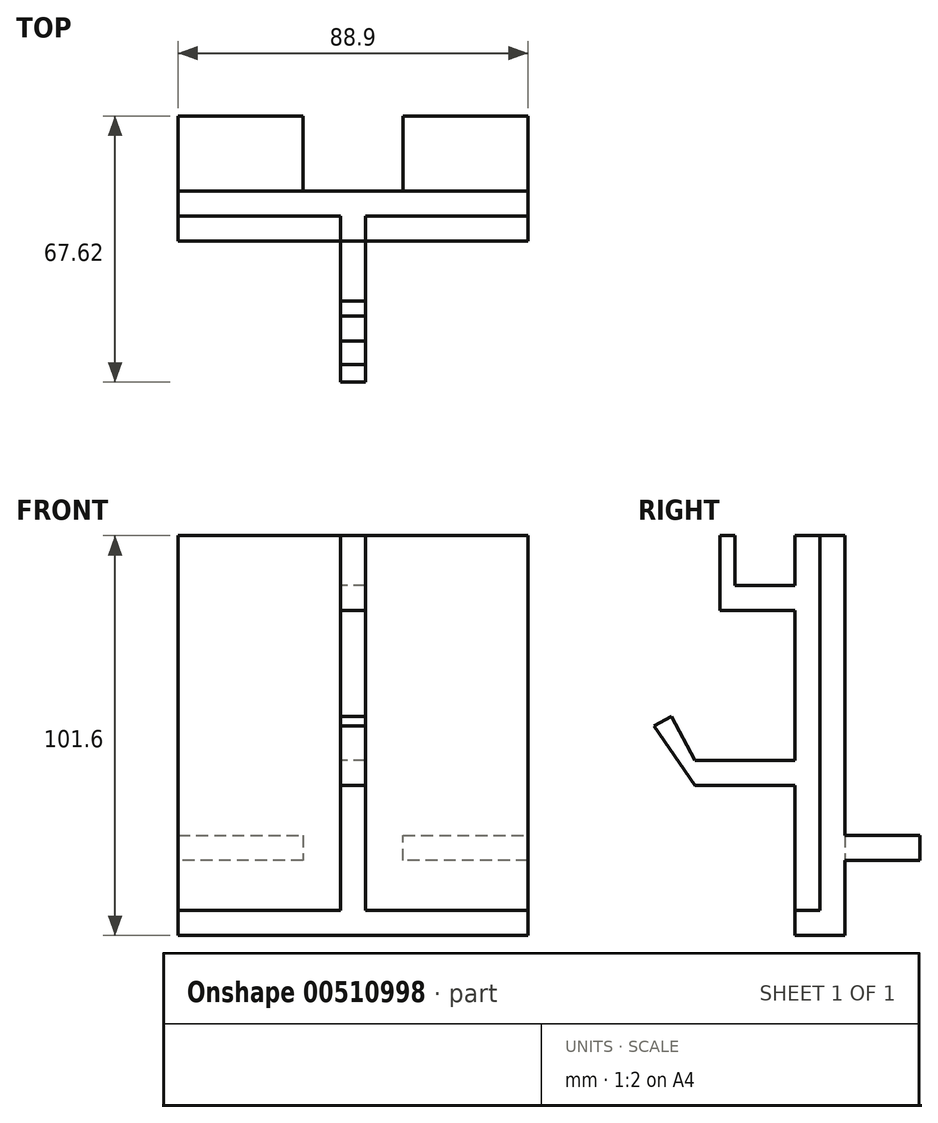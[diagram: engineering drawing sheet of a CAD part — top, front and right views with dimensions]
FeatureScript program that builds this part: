
annotation { "Feature Type Name" : "Feature", "Feature Type Description" : "" }
export const myFeature = defineFeature(function(context is Context, id is Id, definition is map)
    precondition{}
    {
        {
            var Q0;
            Q0=qCreatedBy(makeId("Right.planeOp"),FACE);
            var sketch = newSketch(context, id + "F0", { "sketchPlane" : qUnion([Q0])});
            skLineSegment(sketch, "E0", {"start": v(-3.18, 25.71) * mm, "end": v(-3.17, -75.89) * mm});
            skLineSegment(sketch, "E1", {"start": v(-3.17, -75.89) * mm, "end": v(3.18, -75.89) * mm});
            skLineSegment(sketch, "E2", {"start": v(3.18, -75.89) * mm, "end": v(3.18, 25.71) * mm});
            skLineSegment(sketch, "E3", {"start": v(3.18, 25.71) * mm, "end": v(-3.18, 25.71) * mm});
            skLineSegment(sketch, "E4", {"start": v(-3.17, -31.44) * mm, "end": v(-28.57, -31.44) * mm});
            skLineSegment(sketch, "E5", {"start": v(-28.57, -31.44) * mm, "end": v(-28.57, -37.79) * mm});
            skLineSegment(sketch, "E6", {"start": v(-28.57, -37.79) * mm, "end": v(-3.17, -37.79) * mm});
            skLineSegment(sketch, "E7", {"start": v(-28.57, -31.44) * mm, "end": v(-34.57, -20.24) * mm});
            skLineSegment(sketch, "E8", {"start": v(-34.57, -20.24) * mm, "end": v(-39.05, -22.64) * mm});
            skLineSegment(sketch, "E9", {"start": v(-39.05, -22.64) * mm, "end": v(-28.57, -37.79) * mm});
            skLineSegment(sketch, "E10", {"start": v(-3.18, 13.01) * mm, "end": v(-22.23, 13.01) * mm});
            skLineSegment(sketch, "E11", {"start": v(-22.23, 13.01) * mm, "end": v(-22.23, 6.66) * mm});
            skLineSegment(sketch, "E12", {"start": v(-22.23, 6.66) * mm, "end": v(-3.17, 6.66) * mm});
            skLineSegment(sketch, "E13", {"start": v(-3.18, 6.66) * mm, "end": v(-3.18, 13.01) * mm});
            skSolve(sketch);
        }
        {
            var Q0;
            Q0=makeQuery(id+"F0.imprint","IMPRINT",FACE,{"disambiguationData":[TD([[makeQuery(id+"F0.imprint","IMPRINT",EDGE,{"derivedFrom":sQuery(id+"F0.wireOp",EDGE,"E5")}),-1.0]])]});
            var Q1;
            {var subQ0=sQuery(id+"F0.wireOp",EDGE,"E4");Q1=makeQuery(id+"F0.imprint","IMPRINT",FACE,{"disambiguationData":[TD([[makeQuery(id+"F0.imprint","IMPRINT",EDGE,{"derivedFrom":subQ0}),1.0]])]});}
            var Q2;
            {var subQ0=sQuery(id+"F0.wireOp",EDGE,"E1");Q2=makeQuery(id+"F0.imprint","IMPRINT",FACE,{"disambiguationData":[TD([[makeQuery(id+"F0.imprint","IMPRINT",EDGE,{"derivedFrom":subQ0}),1.0]])]});}
            var Q3;
            Q3=makeQuery(id+"F0.imprint","IMPRINT",FACE,{"disambiguationData":[TD([[makeQuery(id+"F0.imprint","IMPRINT",EDGE,{"derivedFrom":sQuery(id+"F0.wireOp",EDGE,"E10")}),1.0]])]});
            extrude(context, id + "F1", {"entities" : qUnion([Q0, Q1, Q2, Q3]), "depth" : 6.35 * mm, "offsetDistance" : 25.4 * mm});
        }
        {
            var Q0;
            Q0=makeQuery(id+"F1.opExtrude","SWEPT_FACE",FACE,{"disambiguationData":[OSD([sQuery(id+"F0.wireOp",EDGE,"E2")])]});
            var sketch = newSketch(context, id + "F2", { "sketchPlane" : qUnion([Q0])});
            skLineSegment(sketch, "E14", {"start": v(-3.18, 25.71) * mm, "end": v(-47.63, 25.71) * mm});
            skPoint(sketch, "E14.endSnap0", {"position": v(-3.18, 25.71) * mm});
            skLineSegment(sketch, "E15", {"start": v(-47.63, 25.71) * mm, "end": v(-47.62, -75.89) * mm});
            skLineSegment(sketch, "E16", {"start": v(-47.62, -75.89) * mm, "end": v(-6.35, -75.89) * mm});
            skLineSegment(sketch, "E17", {"start": v(-6.35, -75.89) * mm, "end": v(0, -75.89) * mm});
            skLineSegment(sketch, "E18", {"start": v(0, -75.89) * mm, "end": v(41.27, -75.89) * mm});
            skLineSegment(sketch, "E19", {"start": v(41.27, -75.89) * mm, "end": v(41.27, 25.71) * mm});
            skLineSegment(sketch, "E20", {"start": v(41.27, 25.71) * mm, "end": v(-3.18, 25.71) * mm});
            skSolve(sketch);
        }
        {
            var Q0;
            Q0 = qSketchRegion(id + "F2", true);
            extrude(context, id + "F3", {"entities" : qUnion([Q0]), "operationType" : NewBodyOperationType.ADD, "depth" : 6.35 * mm, "offsetDistance" : 25.4 * mm});
        }
        {
            var Q0;
            Q0=makeQuery(id+"F3.opExtrude","CAP_FACE",FACE,{"disambiguationData":[OSD([sQuery(id+"F2.wireOp",EDGE,"E14"),sQuery(id+"F2.wireOp",EDGE,"E15"),sQuery(id+"F2.wireOp",EDGE,"E16"),sQuery(id+"F2.wireOp",EDGE,"E17"),sQuery(id+"F2.wireOp",EDGE,"E18"),sQuery(id+"F2.wireOp",EDGE,"E19"),sQuery(id+"F2.wireOp",EDGE,"E20")])],"isStart":false});
            var sketch = newSketch(context, id + "F4", { "sketchPlane" : qUnion([Q0])});
            skLineSegment(sketch, "E21", {"start": v(-47.62, -56.84) * mm, "end": v(-15.87, -56.84) * mm});
            skLineSegment(sketch, "E22", {"start": v(-15.88, -56.84) * mm, "end": v(-15.88, -50.49) * mm});
            skLineSegment(sketch, "E23", {"start": v(-15.87, -50.49) * mm, "end": v(-47.62, -50.49) * mm});
            skLineSegment(sketch, "E24", {"start": v(-47.62, -50.49) * mm, "end": v(-47.62, -56.84) * mm});
            skLineSegment(sketch, "E25", {"start": v(41.27, -50.49) * mm, "end": v(9.52, -50.49) * mm});
            skLineSegment(sketch, "E26", {"start": v(9.52, -50.49) * mm, "end": v(9.52, -56.84) * mm});
            skLineSegment(sketch, "E27", {"start": v(9.52, -56.84) * mm, "end": v(41.27, -56.84) * mm});
            skLineSegment(sketch, "E28", {"start": v(41.27, -56.84) * mm, "end": v(41.27, -50.49) * mm});
            skSolve(sketch);
        }
        {
            var Q0;
            Q0 = qSketchRegion(id + "F4", true);
            extrude(context, id + "F5", {"entities" : qUnion([Q0]), "operationType" : NewBodyOperationType.ADD, "depth" : 19.05 * mm, "offsetDistance" : 25.4 * mm});
        }
        {
            var Q0;
            {var subQ0=sQuery(id+"F2.wireOp",EDGE,"E20");var subQ1=sQuery(id+"F2.wireOp",EDGE,"E14");var subQ3=sQuery(id+"F2.wireOp",EDGE,"E18");var subQ4=sQuery(id+"F2.wireOp",EDGE,"E17");var subQ5=sQuery(id+"F2.wireOp",EDGE,"E16");var subQ7=sQuery(id+"F2.wireOp",EDGE,"E15");Q0=makeQuery(id+"F3.boolean.opBoolean","SPLIT",FACE,{"disambiguationData":[TD([makeQuery(id+"F3.opExtrude","SWEPT_FACE",FACE,{"disambiguationData":[OSD([subQ7])]})])],"derivedFrom":makeQuery(id+"F3.opExtrude","CAP_FACE",FACE,{"disambiguationData":[OSD([subQ1,subQ7,subQ5,subQ4,subQ3,sQuery(id+"F2.wireOp",EDGE,"E19"),subQ0])],"isStart":true})});}
            var sketch = newSketch(context, id + "F6", { "sketchPlane" : qUnion([Q0])});
            skLineSegment(sketch, "E29", {"start": v(47.62, -69.54) * mm, "end": v(6.35, -69.54) * mm});
            skLineSegment(sketch, "E30", {"start": v(6.35, -69.54) * mm, "end": v(6.35, -75.89) * mm});
            skLineSegment(sketch, "E31", {"start": v(6.35, -75.89) * mm, "end": v(47.62, -75.89) * mm});
            skLineSegment(sketch, "E32", {"start": v(47.62, -75.89) * mm, "end": v(47.62, -69.54) * mm});
            skSolve(sketch);
        }
        {
            var Q0;
            Q0 = qSketchRegion(id + "F6", true);
            extrude(context, id + "F7", {"entities" : qUnion([Q0]), "operationType" : NewBodyOperationType.ADD, "depth" : 6.35 * mm, "offsetDistance" : 25.4 * mm});
        }
        {
            var Q0;
            {var subQ1=sQuery(id+"F2.wireOp",EDGE,"E20");var subQ2=sQuery(id+"F2.wireOp",EDGE,"E14");var subQ4=sQuery(id+"F2.wireOp",EDGE,"E18");var subQ5=sQuery(id+"F2.wireOp",EDGE,"E17");var subQ6=sQuery(id+"F2.wireOp",EDGE,"E16");var subQ7=sQuery(id+"F2.wireOp",EDGE,"E19");Q0=makeQuery(id+"F3.boolean.opBoolean","SPLIT",FACE,{"disambiguationData":[TD([makeQuery(id+"F3.opExtrude","SWEPT_FACE",FACE,{"disambiguationData":[OSD([subQ7])]})])],"derivedFrom":makeQuery(id+"F3.opExtrude","CAP_FACE",FACE,{"disambiguationData":[OSD([subQ2,sQuery(id+"F2.wireOp",EDGE,"E15"),subQ6,subQ5,subQ4,subQ7,subQ1])],"isStart":true})});}
            var sketch = newSketch(context, id + "F8", { "sketchPlane" : qUnion([Q0])});
            skLineSegment(sketch, "E33", {"start": v(0, -69.53) * mm, "end": v(-41.27, -69.53) * mm});
            skLineSegment(sketch, "E34", {"start": v(-41.27, -69.53) * mm, "end": v(-41.27, -75.89) * mm});
            skLineSegment(sketch, "E35", {"start": v(-41.27, -75.89) * mm, "end": v(0, -75.89) * mm});
            skLineSegment(sketch, "E36", {"start": v(0, -75.89) * mm, "end": v(0, -69.53) * mm});
            skSolve(sketch);
        }
        {
            var Q0;
            Q0 = qSketchRegion(id + "F8", true);
            extrude(context, id + "F9", {"entities" : qUnion([Q0]), "operationType" : NewBodyOperationType.ADD, "depth" : 6.35 * mm, "offsetDistance" : 25.4 * mm});
        }
        {
            var Q0;
            Q0=makeQuery(id+"F1.opExtrude","SWEPT_FACE",FACE,{"disambiguationData":[OSD([sQuery(id+"F0.wireOp",EDGE,"E10")])]});
            var sketch = newSketch(context, id + "F10", { "sketchPlane" : qUnion([Q0])});
            skLineSegment(sketch, "E37", {"start": v(0, -18.41) * mm, "end": v(6.35, -18.41) * mm});
            skLineSegment(sketch, "E38", {"start": v(6.35, -18.41) * mm, "end": v(6.35, -22.23) * mm});
            skLineSegment(sketch, "E39", {"start": v(6.35, -22.23) * mm, "end": v(0, -22.23) * mm});
            skLineSegment(sketch, "E40", {"start": v(0, -22.23) * mm, "end": v(0, -18.41) * mm});
            skSolve(sketch);
        }
        {
            var Q0;
            Q0 = qSketchRegion(id + "F10", true);
            extrude(context, id + "F11", {"entities" : qUnion([Q0]), "operationType" : NewBodyOperationType.ADD, "depth" : 12.7 * mm, "offsetDistance" : 25.4 * mm});
        }
    });
